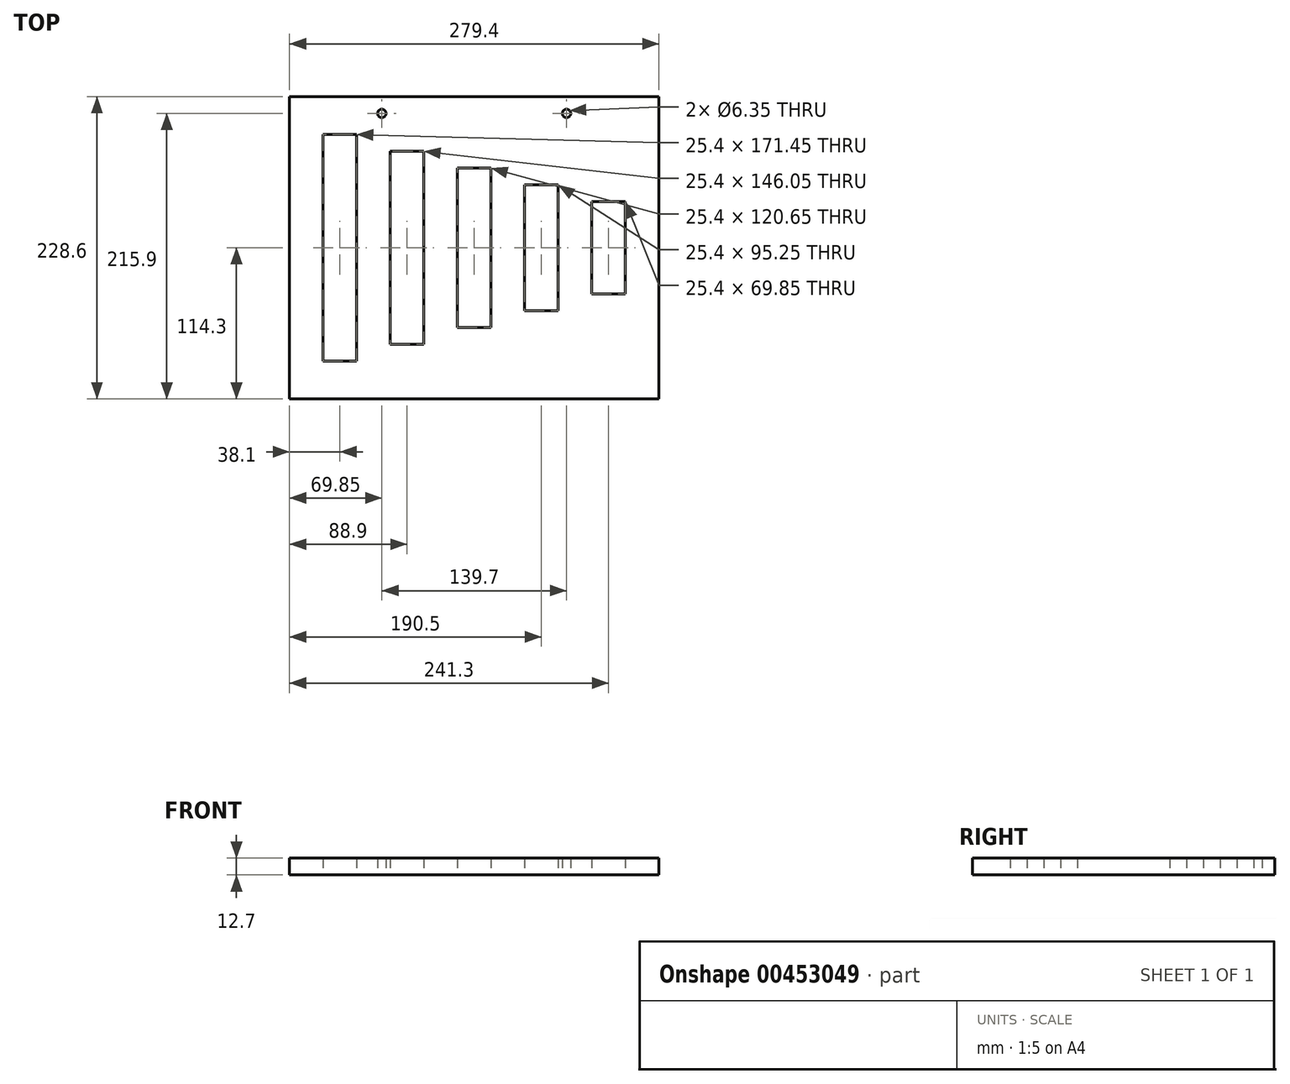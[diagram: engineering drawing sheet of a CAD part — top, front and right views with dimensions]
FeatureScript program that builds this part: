
annotation { "Feature Type Name" : "Feature", "Feature Type Description" : "" }
export const myFeature = defineFeature(function(context is Context, id is Id, definition is map)
    precondition{}
    {
        {
            var Q0;
            Q0=qCreatedBy(makeId("Top.planeOp"),FACE);
            var sketch = newSketch(context, id + "F0", { "sketchPlane" : qUnion([Q0])});
            skLineSegment(sketch, "E0.bottom", {"start": v(-190.5, -85.72) * mm, "end": v(-215.9, -85.72) * mm});
            skLineSegment(sketch, "E0.top", {"start": v(-190.5, 85.73) * mm, "end": v(-215.9, 85.73) * mm});
            skLineSegment(sketch, "E0.left", {"start": v(-190.5, -85.72) * mm, "end": v(-190.5, 85.73) * mm});
            skLineSegment(sketch, "E0.right", {"start": v(-215.9, -85.72) * mm, "end": v(-215.9, 85.73) * mm});
            skPoint(sketch, "E0.middle", {"position": v(-203.2, 0) * mm});
            skLineSegment(sketch, "E1.bottom", {"start": v(-139.7, -73.03) * mm, "end": v(-165.1, -73.03) * mm});
            skLineSegment(sketch, "E1.top", {"start": v(-139.7, 73.02) * mm, "end": v(-165.1, 73.02) * mm});
            skLineSegment(sketch, "E1.left", {"start": v(-139.7, -73.03) * mm, "end": v(-139.7, 73.02) * mm});
            skLineSegment(sketch, "E1.right", {"start": v(-165.1, -73.03) * mm, "end": v(-165.1, 73.02) * mm});
            skPoint(sketch, "E1.middle", {"position": v(-152.4, 0) * mm});
            skLineSegment(sketch, "E2.bottom", {"start": v(-88.9, -60.33) * mm, "end": v(-114.3, -60.33) * mm});
            skLineSegment(sketch, "E2.top", {"start": v(-88.9, 60.32) * mm, "end": v(-114.3, 60.32) * mm});
            skLineSegment(sketch, "E2.left", {"start": v(-88.9, -60.33) * mm, "end": v(-88.9, 60.32) * mm});
            skLineSegment(sketch, "E2.right", {"start": v(-114.3, -60.33) * mm, "end": v(-114.3, 60.32) * mm});
            skPoint(sketch, "E2.middle", {"position": v(-101.6, 0) * mm});
            skLineSegment(sketch, "E3.bottom", {"start": v(-38.1, -47.63) * mm, "end": v(-63.5, -47.63) * mm});
            skLineSegment(sketch, "E3.top", {"start": v(-38.1, 47.62) * mm, "end": v(-63.5, 47.62) * mm});
            skLineSegment(sketch, "E3.left", {"start": v(-38.1, -47.63) * mm, "end": v(-38.1, 47.62) * mm});
            skLineSegment(sketch, "E3.right", {"start": v(-63.5, -47.63) * mm, "end": v(-63.5, 47.62) * mm});
            skPoint(sketch, "E3.middle", {"position": v(-50.8, 0) * mm});
            skLineSegment(sketch, "E4.bottom", {"start": v(12.7, -34.93) * mm, "end": v(-12.7, -34.93) * mm});
            skLineSegment(sketch, "E4.top", {"start": v(12.7, 34.93) * mm, "end": v(-12.7, 34.93) * mm});
            skLineSegment(sketch, "E4.left", {"start": v(12.7, -34.93) * mm, "end": v(12.7, 34.92) * mm});
            skLineSegment(sketch, "E4.right", {"start": v(-12.7, -34.93) * mm, "end": v(-12.7, 34.93) * mm});
            skPoint(sketch, "E4.middle", {"position": v(0, 0) * mm});
            skLineSegment(sketch, "E5.bottom", {"start": v(-241.3, 114.3) * mm, "end": v(38.1, 114.3) * mm});
            skLineSegment(sketch, "E5.top", {"start": v(-241.3, -114.3) * mm, "end": v(38.1, -114.3) * mm});
            skLineSegment(sketch, "E5.left", {"start": v(-241.3, 114.3) * mm, "end": v(-241.3, -114.3) * mm});
            skLineSegment(sketch, "E5.right", {"start": v(38.1, 114.3) * mm, "end": v(38.1, -114.3) * mm});
            skLineSegment(sketch, "E6", {"start": v(-241.3, 0) * mm, "end": v(-253, 0) * mm, "construction": true});
            skLineSegment(sketch, "E7", {"start": v(-241.3, 114.3) * mm, "end": v(-241.3, 101.6) * mm, "construction": true});
            skLineSegment(sketch, "E8", {"start": v(-241.3, 101.6) * mm, "end": v(38.1, 101.6) * mm, "construction": true});
            skLineSegment(sketch, "E9", {"start": v(-101.6, 101.6) * mm, "end": v(-171.45, 101.6) * mm, "construction": true});
            skLineSegment(sketch, "E10", {"start": v(-101.6, 101.6) * mm, "end": v(-31.75, 101.6) * mm, "construction": true});
            skCircle(sketch, "E11", {"center": v(-171.45, 101.6) * mm, "radius": 3.18 * mm});
            skCircle(sketch, "E12", {"center": v(-31.75, 101.6) * mm, "radius": 3.18 * mm});
            skSolve(sketch);
        }
        {
            var Q0;
            Q0=makeQuery(id+"F0.imprint","IMPRINT",FACE,{"disambiguationData":[TD([[makeQuery(id+"F0.imprint","IMPRINT",EDGE,{"derivedFrom":sQuery(id+"F0.wireOp",EDGE,"E0.bottom")}),1.0]])]});
            extrude(context, id + "F1", {"entities" : qUnion([Q0]), "depth" : 12.7 * mm, "offsetDistance" : 25.4 * mm});
        }
    });
